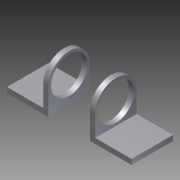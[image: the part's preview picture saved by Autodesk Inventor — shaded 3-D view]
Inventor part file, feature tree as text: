
AUTODESK INVENTOR PART (.ipt)
format: ipt  version: 2012 (Build 160160000, 160)  size: 113,152 bytes
history: native  units: in
note: dims shown in document units (in); Inventor stores cm internally (conversion verified against a paired STEP export)
features: extrude x2, sketch x2
ambient origin geometry x8: Origin, YZ Plane, XZ Plane, XY Plane, X Axis, Y Axis, Z Axis, Center Point
bodies: Solid1 (feature_tree)
feature tree (4):
  extrude  "Extrusion1"  Depth=0.125in
  extrude  "Extrusion2"  Depth=1.125in
  sketch  "Sketch1"  dims[d0=0.125in d1=0.125in]
  sketch  "Sketch2"  dims[d2=1.0in d3=1.125in d4=0.5in d5=1.0in d6=0.0in d7=0.875in d8=0.625in d9=0.5in d10=1.0in d11=0.0in]
